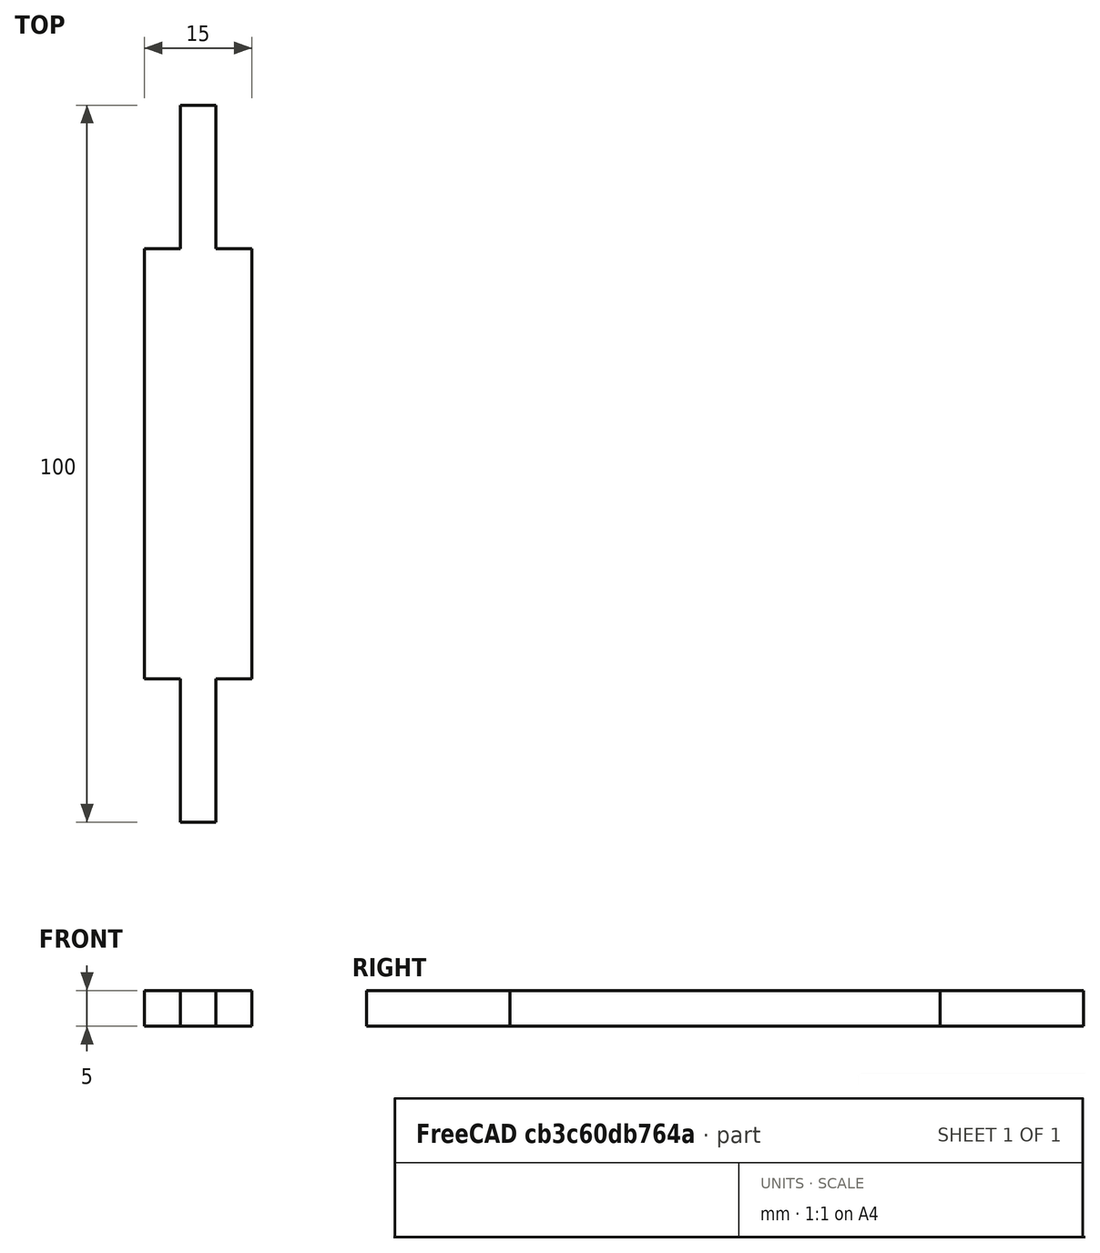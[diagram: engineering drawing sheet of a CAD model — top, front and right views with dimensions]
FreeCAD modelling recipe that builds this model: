
FCSTD DOCUMENT  (FreeCAD 0.16R6712 (Git))
Label: AssemblerWire
License: All rights reserved
LicenseURL: http://en.wikipedia.org/wiki/All_rights_reserved
objects: Sketcher::SketchObject×1, PartDesign::Pad×1
note: 3 computed .brp shape members not serialized (recipe doc carries the construction recipe); baked Part::Feature solids carry a one-line shape summary decoded from their .brp

FEATURE [Sketcher::SketchObject] Sketch025
  Placement = pos=(0,36,115) rot=(0,0,1;0rad)
  sketch-geometry (12):
    g0: LineSegment StartX=7.5 StartY=30 StartZ=0 EndX=7.5 EndY=-30 EndZ=0
    g1: LineSegment StartX=2.5 StartY=-50 StartZ=0 EndX=-2.5 EndY=-50 EndZ=0
    g2: LineSegment StartX=-7.5 StartY=-30 StartZ=0 EndX=-7.5 EndY=30 EndZ=0
    g3: LineSegment StartX=-2.5 StartY=30 StartZ=0 EndX=-7.5 EndY=30 EndZ=0
    g4: LineSegment StartX=2.5 StartY=30 StartZ=0 EndX=7.5 EndY=30 EndZ=0
    g5: LineSegment StartX=-2.5 StartY=30 StartZ=0 EndX=-2.5 EndY=50 EndZ=0
    g6: LineSegment StartX=2.5 StartY=30 StartZ=0 EndX=2.5 EndY=50 EndZ=0
    g7: LineSegment StartX=-2.5 StartY=-30 StartZ=0 EndX=-7.5 EndY=-30 EndZ=0
    g8: LineSegment StartX=2.5 StartY=-30 StartZ=0 EndX=7.5 EndY=-30 EndZ=0
    g9: LineSegment StartX=-2.5 StartY=-30 StartZ=0 EndX=-2.5 EndY=-50 EndZ=0
    g10: LineSegment StartX=2.5 StartY=-30 StartZ=0 EndX=2.5 EndY=-50 EndZ=0
    g11: LineSegment StartX=-2.5 StartY=50 StartZ=0 EndX=2.5 EndY=50 EndZ=0
  constraints (38):
    c: Horizontal(g1)
    c: Vertical(g0)
    c: Vertical(g2)
    c: Horizontal(g3)
    c: Horizontal(g4)
    c: Vertical(g5)
    c: Vertical(g6)
    c: Symmetric(g7,g3,g-1)
    c: Coincident(g3,g5)
    c: Horizontal(g7)
    c: Horizontal(g8)
    c: Vertical(g9)
    c: Vertical(g10)
    c: Coincident(g2,g7)
    c: Coincident(g1,g9)
    c: Coincident(g1,g10)
    c: Coincident(g0,g8)
    c: Symmetric(g1,g5,g-1)
    c: Equal(g3,g7)
    c: Equal(g4,g8)
    c: Coincident(g2,g3)
    c: Coincident(g0,g4)
    c: Coincident(g11,g5)
    c: Coincident(g11,g6)
    c: Horizontal(g11)
    c: Symmetric(g8,g7,g-2)
    c: Symmetric(g1,g1,g-2)
    c: Symmetric(g6,g5,g-2)
    c: Equal(g8,g7)
    c: Equal(g4,g3)
    c: DistanceY(g2,g2) = 60
    c: DistanceX(g1,g1) = 5
    c: DistanceY(g9,g9) = 20
    c: Coincident(g7,g9)
    c: DistanceX(g7,g7) = 5
    c: Coincident(g6,g4)
    c: Coincident(g10,g8)
    c: Symmetric(g4,g3,g-2)
FEATURE [PartDesign::Pad] Pad020  label="TopAssemblerWire"
  Length = 5
  Length2 = 100
  Placement = pos=(0,36,115) rot=(0,0,1;0rad)
  Sketch = -> Sketch025
  Type = 0
